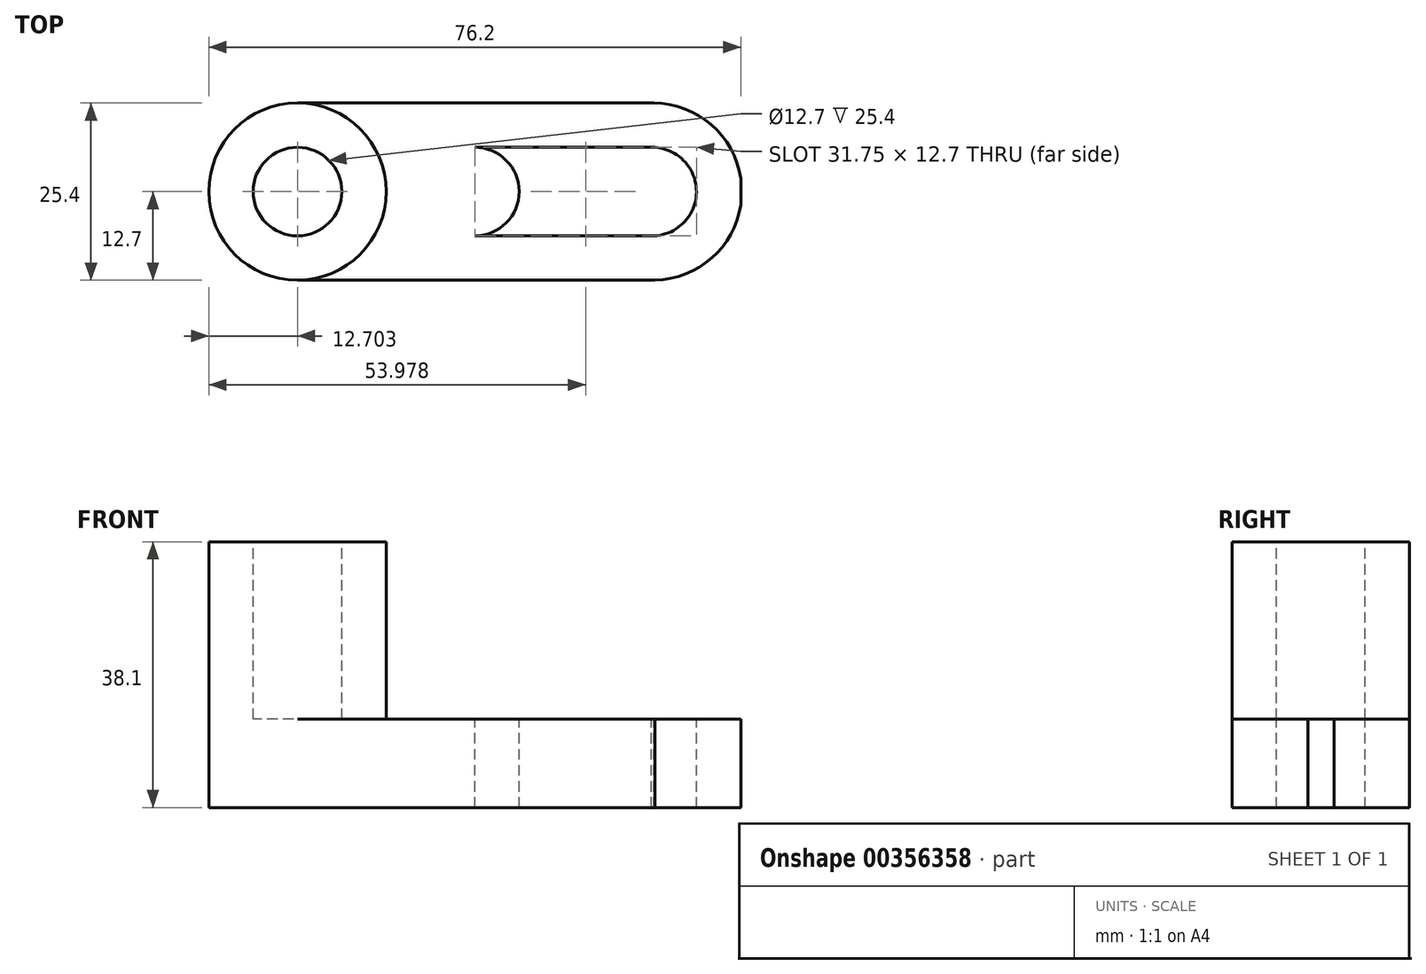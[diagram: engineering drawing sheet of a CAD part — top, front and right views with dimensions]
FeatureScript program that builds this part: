
annotation { "Feature Type Name" : "Feature", "Feature Type Description" : "" }
export const myFeature = defineFeature(function(context is Context, id is Id, definition is map)
    precondition{}
    {
        {
            var Q0;
            Q0=qCreatedBy(makeId("Front.planeOp"),FACE);
            var sketch = newSketch(context, id + "F0", { "sketchPlane" : qUnion([Q0])});
            skLineSegment(sketch, "E0.bottom", {"start": v(-35.24, 0) * mm, "end": v(40.96, 0) * mm});
            skLineSegment(sketch, "E0.top", {"start": v(-35.24, 12.7) * mm, "end": v(40.96, 12.7) * mm});
            skLineSegment(sketch, "E0.left", {"start": v(-35.24, 0) * mm, "end": v(-35.24, 12.7) * mm});
            skLineSegment(sketch, "E0.right", {"start": v(40.96, 0) * mm, "end": v(40.96, 12.7) * mm});
            skSolve(sketch);
        }
        {
            var Q0;
            Q0=makeQuery(id+"F0.imprint","IMPRINT",FACE,{"disambiguationData":[TD([[makeQuery(id+"F0.imprint","IMPRINT",EDGE,{"derivedFrom":sQuery(id+"F0.wireOp",EDGE,"E0.bottom")}),1.0]])]});
            extrude(context, id + "F1", {"entities" : qUnion([Q0]), "depth" : 25.4 * mm});
        }
        {
            var Q0;
            Q0=makeQuery(id+"F1.opExtrude","SWEPT_FACE",FACE,{"disambiguationData":[OSD([sQuery(id+"F0.wireOp",EDGE,"E0.top")])]});
            var sketch = newSketch(context, id + "F2", { "sketchPlane" : qUnion([Q0])});
            skCircle(sketch, "E1", {"center": v(2.86, -12.7) * mm, "radius": 6.35 * mm});
            skCircle(sketch, "E2", {"center": v(28.26, -12.7) * mm, "radius": 6.35 * mm});
            skLineSegment(sketch, "E3", {"start": v(2.86, -6.35) * mm, "end": v(28.26, -6.35) * mm});
            skLineSegment(sketch, "E4", {"start": v(28.15, -19.05) * mm, "end": v(2.86, -19.05) * mm});
            skArc(sketch, "E5", {"start": v(28.15, -25.4) * mm, "mid": v(41.1, -12.76) * mm, "end": v(28.26, 0) * mm});
            skSolve(sketch);
        }
        {
            var Q0;
            {var subQ0=sQuery(id+"F2.wireOp",EDGE,"E1");var subQ2=makeQuery(id+"F2.imprint","IMPRINT",VERTEX,{"derivedFrom":subQ0});Q0=makeQuery(id+"F2.imprint","IMPRINT",FACE,{"disambiguationData":[TD([[makeQuery(id+"F2.imprint","IMPRINT",EDGE,{"disambiguationData":[TD([[subQ2,1.0]])],"derivedFrom":subQ0}),1.0]])]});}
            var Q1;
            {var subQ0=sQuery(id+"F2.wireOp",EDGE,"E3");Q1=makeQuery(id+"F2.imprint","IMPRINT",FACE,{"disambiguationData":[TD([[makeQuery(id+"F2.imprint","IMPRINT",EDGE,{"derivedFrom":subQ0}),-1.0]])]});}
            var Q2;
            {var subQ0=sQuery(id+"F2.wireOp",EDGE,"E2");var subQ1=makeQuery(id+"F2.imprint","INTERSECT",VERTEX,{"derivedFrom":[subQ0,sQuery(id+"F2.wireOp",EDGE,"E3")]});Q2=makeQuery(id+"F2.imprint","IMPRINT",FACE,{"disambiguationData":[TD([[makeQuery(id+"F2.imprint","IMPRINT",EDGE,{"disambiguationData":[TD([[subQ1,-1.0]])],"derivedFrom":subQ0}),1.0]])]});}
            var Q3;
            {var subQ0=sQuery(id+"F2.wireOp",EDGE,"E5");var subQ1=sQuery(id+"F0.wireOp",EDGE,"E0.top");var subQ4=makeQuery(id+"F1.opExtrude","CAP_EDGE",EDGE,{"disambiguationData":[OSD([subQ1])],"isStart":true});var subQ5=makeQuery(id+"F2.imprint","INTERSECT",VERTEX,{"disambiguationData":[OD(1.0)],"derivedFrom":[subQ4,subQ0]});Q3=makeQuery(id+"F2.imprint","IMPRINT",FACE,{"disambiguationData":[TD([[makeQuery(id+"F2.imprint","IMPRINT",EDGE,{"disambiguationData":[TD([[subQ5,1.0]])],"derivedFrom":subQ0}),-1.0]])]});}
            var Q4;
            {var subQ0=sQuery(id+"F2.wireOp",EDGE,"E5");var subQ1=sQuery(id+"F0.wireOp",EDGE,"E0.top");var subQ2=makeQuery(id+"F1.opExtrude","CAP_EDGE",EDGE,{"disambiguationData":[OSD([subQ1])],"isStart":false});var subQ3=makeQuery(id+"F2.imprint","INTERSECT",VERTEX,{"disambiguationData":[OD(1.0)],"derivedFrom":[subQ2,subQ0]});Q4=makeQuery(id+"F2.imprint","IMPRINT",FACE,{"disambiguationData":[TD([[makeQuery(id+"F2.imprint","IMPRINT",EDGE,{"disambiguationData":[TD([[subQ3,-1.0]])],"derivedFrom":subQ0}),-1.0]])]});}
            extrude(context, id + "F3", {"entities" : qUnion([Q0, Q1, Q2, Q3, Q4]), "operationType" : NewBodyOperationType.REMOVE, "oppositeDirection" : true, "depth" : 12.7 * mm});
        }
        {
            var Q0;
            Q0=makeQuery(id+"F1.opExtrude","SWEPT_FACE",FACE,{"disambiguationData":[OSD([sQuery(id+"F0.wireOp",EDGE,"E0.top")])]});
            var sketch = newSketch(context, id + "F4", { "sketchPlane" : qUnion([Q0])});
            skCircle(sketch, "E6", {"center": v(-22.54, -12.7) * mm, "radius": 12.7 * mm});
            skSolve(sketch);
        }
        {
            var Q0;
            {var subQ0=sQuery(id+"F4.wireOp",EDGE,"E6");var subQ1=sQuery(id+"F0.wireOp",EDGE,"E0.top");var subQ3=makeQuery(id+"F4.imprint","INTERSECT",VERTEX,{"derivedFrom":[makeQuery(id+"F1.opExtrude","CAP_EDGE",EDGE,{"disambiguationData":[OSD([subQ1])],"isStart":true}),subQ0]});Q0=makeQuery(id+"F4.imprint","IMPRINT",FACE,{"disambiguationData":[TD([[makeQuery(id+"F4.imprint","IMPRINT",EDGE,{"disambiguationData":[TD([[subQ3,1.0]])],"derivedFrom":subQ0}),1.0]])]});}
            extrude(context, id + "F5", {"entities" : qUnion([Q0]), "operationType" : NewBodyOperationType.ADD, "depth" : 25.4 * mm});
        }
        {
            var Q0;
            {var subQ0=sQuery(id+"F0.wireOp",EDGE,"E0.left");var subQ1=sQuery(id+"F0.wireOp",EDGE,"E0.top");var subQ2=makeQuery(id+"F1.opExtrude","SWEPT_FACE",FACE,{"disambiguationData":[OSD([subQ1])]});Q0=makeQuery(id+"F5.boolean.opBoolean","SPLIT",FACE,{"disambiguationData":[TD([makeQuery(id+"F1.opExtrude","CAP_FACE",FACE,{"disambiguationData":[OSD([sQuery(id+"F0.wireOp",EDGE,"E0.bottom"),subQ1,subQ0,sQuery(id+"F0.wireOp",EDGE,"E0.right")])],"isStart":true}),subQ2,makeQuery(id+"F1.opExtrude","SWEPT_FACE",FACE,{"disambiguationData":[OSD([subQ0])]}),makeQuery(id+"F5.opExtrude","SWEPT_FACE",FACE,{"disambiguationData":[OSD([sQuery(id+"F4.wireOp",EDGE,"E6")])]})])],"derivedFrom":subQ2});}
            var Q1;
            {var subQ0=sQuery(id+"F0.wireOp",EDGE,"E0.left");var subQ1=sQuery(id+"F0.wireOp",EDGE,"E0.top");var subQ2=makeQuery(id+"F1.opExtrude","SWEPT_FACE",FACE,{"disambiguationData":[OSD([subQ1])]});Q1=makeQuery(id+"F5.boolean.opBoolean","SPLIT",FACE,{"disambiguationData":[TD([makeQuery(id+"F1.opExtrude","CAP_FACE",FACE,{"disambiguationData":[OSD([sQuery(id+"F0.wireOp",EDGE,"E0.bottom"),subQ1,subQ0,sQuery(id+"F0.wireOp",EDGE,"E0.right")])],"isStart":false}),subQ2,makeQuery(id+"F1.opExtrude","SWEPT_FACE",FACE,{"disambiguationData":[OSD([subQ0])]}),makeQuery(id+"F5.opExtrude","SWEPT_FACE",FACE,{"disambiguationData":[OSD([sQuery(id+"F4.wireOp",EDGE,"E6")])]})])],"derivedFrom":subQ2});}
            extrude(context, id + "F6", {"entities" : qUnion([Q0, Q1]), "operationType" : NewBodyOperationType.REMOVE, "oppositeDirection" : true, "depth" : 12.7 * mm});
        }
        {
            var Q0;
            Q0=makeQuery(id+"F5.opExtrude","CAP_FACE",FACE,{"disambiguationData":[OSD([sQuery(id+"F4.wireOp",EDGE,"E6")])],"isStart":false});
            var sketch = newSketch(context, id + "F7", { "sketchPlane" : qUnion([Q0])});
            skCircle(sketch, "E7", {"center": v(-22.54, -12.7) * mm, "radius": 6.35 * mm});
            skSolve(sketch);
        }
        {
            var Q0;
            Q0=makeQuery(id+"F7.imprint","IMPRINT",FACE,{"disambiguationData":[TD([[makeQuery(id+"F7.imprint","IMPRINT",EDGE,{"derivedFrom":sQuery(id+"F7.wireOp",EDGE,"E7")}),1.0]])]});
            extrude(context, id + "F8", {"entities" : qUnion([Q0]), "operationType" : NewBodyOperationType.REMOVE, "oppositeDirection" : true, "depth" : 25.4 * mm});
        }
    });
